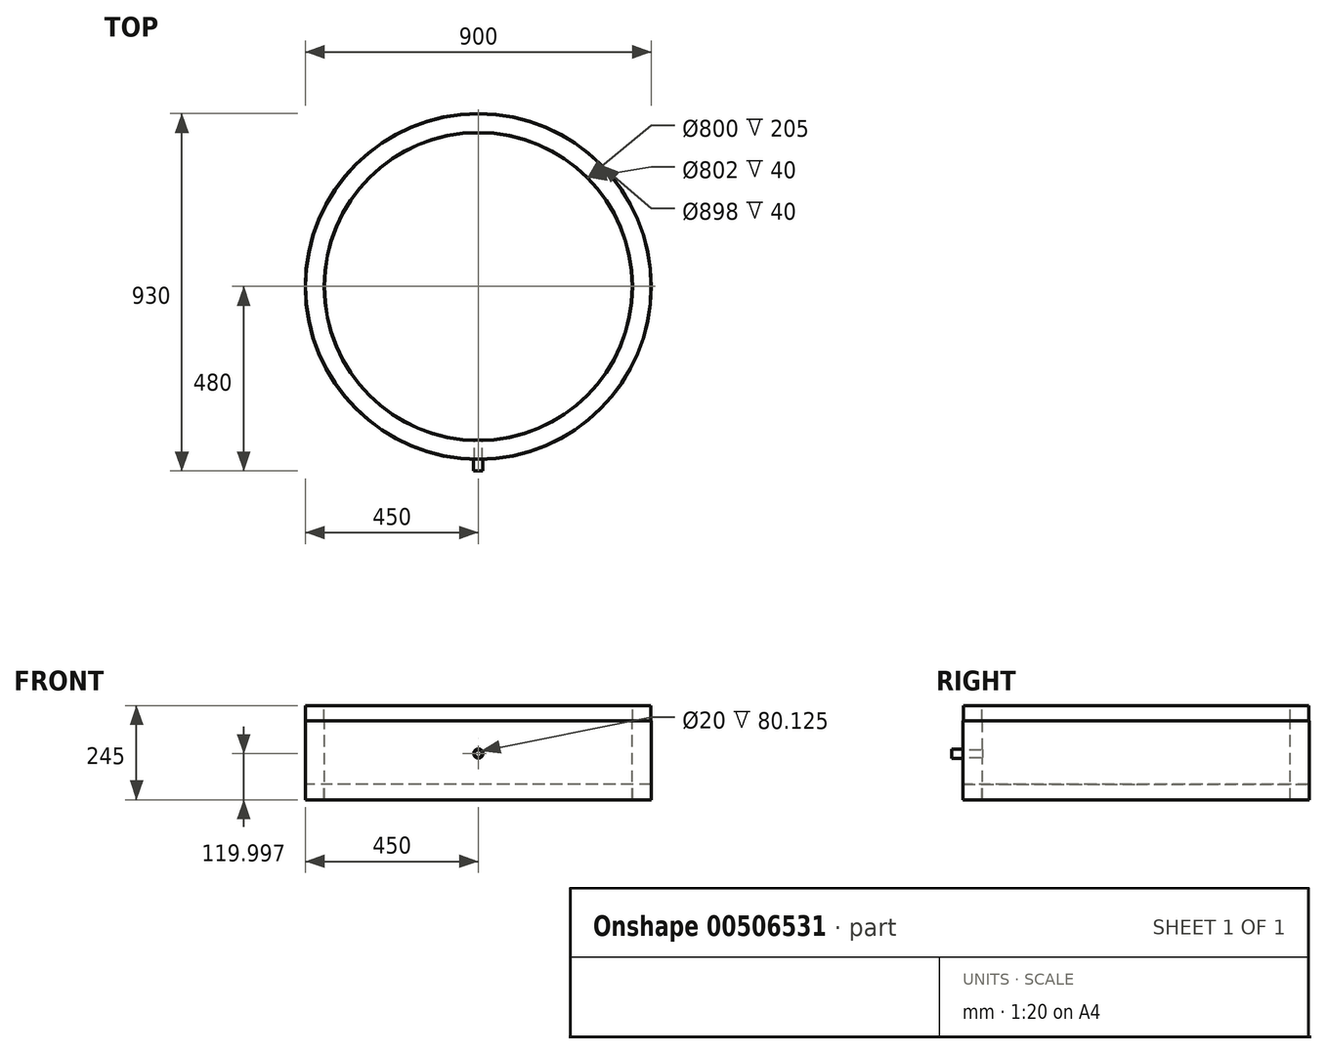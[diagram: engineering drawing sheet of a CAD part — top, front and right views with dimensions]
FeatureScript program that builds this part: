
annotation { "Feature Type Name" : "Feature", "Feature Type Description" : "" }
export const myFeature = defineFeature(function(context is Context, id is Id, definition is map)
    precondition{}
    {
        {
            var Q0;
            Q0=qCreatedBy(makeId("Front.planeOp"),FACE);
            var sketch = newSketch(context, id + "F0", { "sketchPlane" : qUnion([Q0])});
            skLineSegment(sketch, "E0", {"start": v(0, 74.87) * mm, "end": v(0, -73.71) * mm, "construction": true});
            skLineSegment(sketch, "E1", {"start": v(0, 374.84) * mm, "end": v(0, -528.94) * mm, "construction": true});
            skLineSegment(sketch, "E2", {"start": v(-400, -489.75) * mm, "end": v(-400, -284.75) * mm});
            skLineSegment(sketch, "E3", {"start": v(-400, -284.75) * mm, "end": v(-401, -284.75) * mm});
            skLineSegment(sketch, "E4", {"start": v(-401, -284.75) * mm, "end": v(-401, -244.75) * mm});
            skLineSegment(sketch, "E5", {"start": v(-401, -244.75) * mm, "end": v(-449, -244.75) * mm});
            skLineSegment(sketch, "E6", {"start": v(-449, -244.75) * mm, "end": v(-449, -284.75) * mm});
            skLineSegment(sketch, "E7", {"start": v(-449, -284.75) * mm, "end": v(-450, -284.75) * mm});
            skLineSegment(sketch, "E8", {"start": v(-450, -284.75) * mm, "end": v(-450, -489.75) * mm});
            skLineSegment(sketch, "E9", {"start": v(-450, -489.75) * mm, "end": v(-449, -489.75) * mm});
            skLineSegment(sketch, "E10", {"start": v(-449, -489.75) * mm, "end": v(-449, -449.75) * mm});
            skLineSegment(sketch, "E11", {"start": v(-449, -449.75) * mm, "end": v(-401, -449.75) * mm});
            skLineSegment(sketch, "E12", {"start": v(-401, -449.75) * mm, "end": v(-401, -489.75) * mm});
            skLineSegment(sketch, "E13", {"start": v(-401, -489.75) * mm, "end": v(-400, -489.75) * mm});
            skSolve(sketch);
        }
        {
            var Q0;
            Q0=qSketchRegion(id+"F0",true);
            var Q1;
            Q1=sQuery(id+"F0.wireOp",EDGE,"E1");
            revolve(context, id + "F1", {"entities" : qUnion([Q0]), "axis" : qUnion([Q1]), "revolveType" : RevolveType.FULL});
        }
        {
            var Q0;
            Q0=qCreatedBy(makeId("Front.planeOp"),FACE);
            var sketch = newSketch(context, id + "F2", { "sketchPlane" : qUnion([Q0])});
            skLineSegment(sketch, "E14", {"start": v(0, 0) * mm, "end": v(0, -739.5) * mm, "construction": true});
            skCircle(sketch, "E15", {"center": v(0, -369.75) * mm, "radius": 10 * mm});
            skLineSegment(sketch, "E16.0", {"start": v(-449, -244.75) * mm, "end": v(449, -244.75) * mm, "construction": true});
            skSolve(sketch);
        }
        {
            var Q0;
            Q0=qSketchRegion(id+"F2",true);
            extrude(context, id + "F3", {"entities" : qUnion([Q0]), "operationType" : NewBodyOperationType.REMOVE, "depth" : 661 * mm});
        }
        {
            var Q0;
            Q0=qCreatedBy(makeId("Front.planeOp"),FACE);
            cPlane(context, id + "F4", {"entities" : qUnion([Q0]), "cplaneType" : CPlaneType.OFFSET, "offset" : 400 * mm, "width" : 150 * mm, "height" : 150 * mm});
        }
        {
            var Q0;
            Q0=qCreatedBy(id+"F4.planeOp",FACE);
            var sketch = newSketch(context, id + "F5", { "sketchPlane" : qUnion([Q0])});
            skLineSegment(sketch, "E17", {"start": v(0, 0) * mm, "end": v(0, -620.93) * mm, "construction": true});
            skLineSegment(sketch, "E18.0", {"start": v(-449, -244.75) * mm, "end": v(449, -244.75) * mm, "construction": true});
            skCircle(sketch, "E19.0", {"center": v(0, -369.75) * mm, "radius": 10 * mm});
            skCircle(sketch, "E20", {"center": v(0, -369.75) * mm, "radius": 12 * mm});
            skSolve(sketch);
        }
        {
            var Q0;
            Q0=qSketchRegion(id+"F5",true);
            extrude(context, id + "F6", {"entities" : qUnion([Q0]), "operationType" : NewBodyOperationType.ADD, "depth" : 80 * mm});
        }
    });
